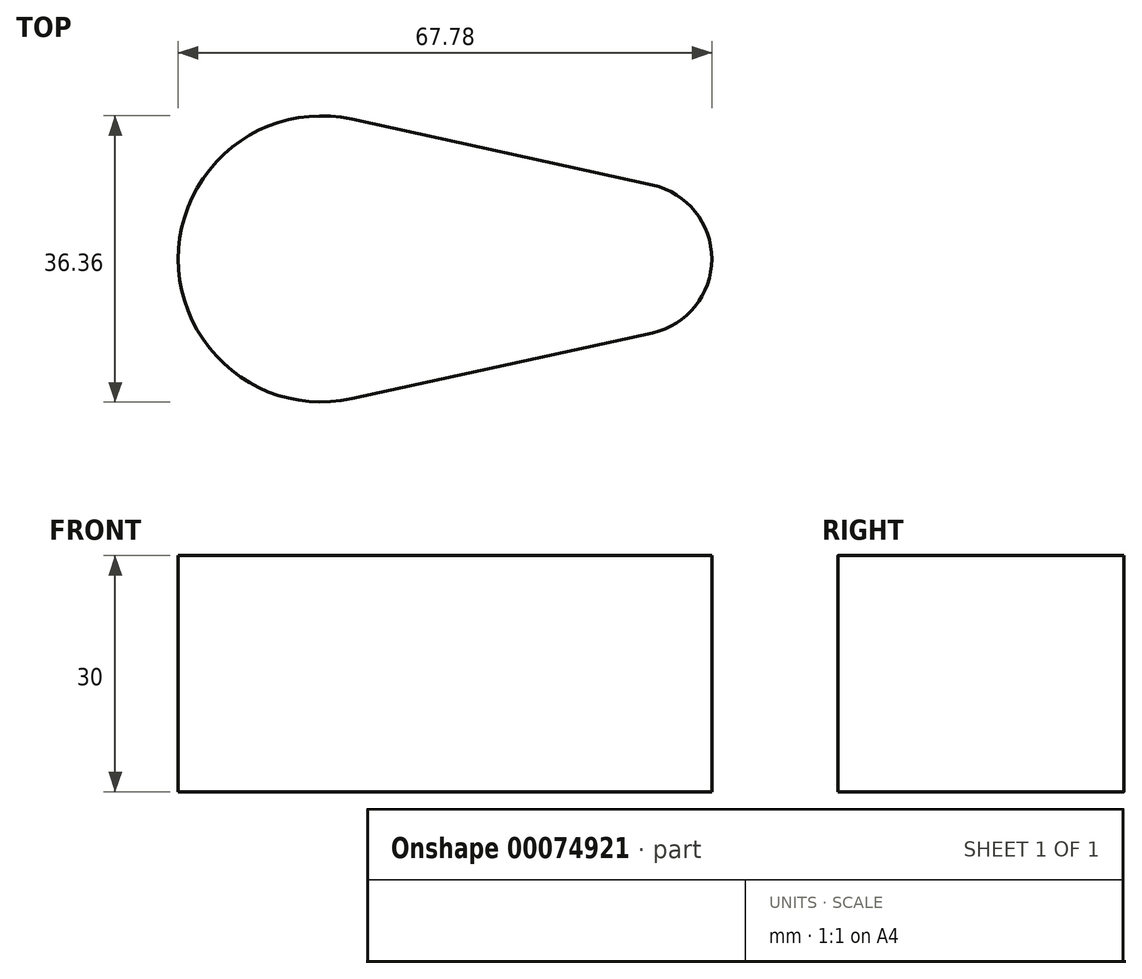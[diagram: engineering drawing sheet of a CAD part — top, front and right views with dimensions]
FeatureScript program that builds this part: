
annotation { "Feature Type Name" : "Feature", "Feature Type Description" : "" }
export const myFeature = defineFeature(function(context is Context, id is Id, definition is map)
    precondition{}
    {
        {
            var Q0;
            Q0=qCreatedBy(makeId("Top.planeOp"),FACE);
            var sketch = newSketch(context, id + "F0", { "sketchPlane" : qUnion([Q0])});
            skArc(sketch, "E0", {"start": v(3.9, 17.75) * mm, "mid": v(-18.18, 0) * mm, "end": v(3.9, -17.75) * mm});
            skArc(sketch, "E1", {"start": v(42.06, -9.38) * mm, "mid": v(49.6, 0) * mm, "end": v(42.06, 9.38) * mm});
            skLineSegment(sketch, "E2", {"start": v(3.9, 17.75) * mm, "end": v(42.06, 9.38) * mm});
            skLineSegment(sketch, "E3", {"start": v(3.9, -17.75) * mm, "end": v(42.06, -9.38) * mm});
            skSolve(sketch);
        }
        {
            var Q0;
            Q0 = qSketchRegion(id + "F0", true);
            extrude(context, id + "F1", {"entities" : qUnion([Q0]), "depth" : 30 * mm});
        }
    });
